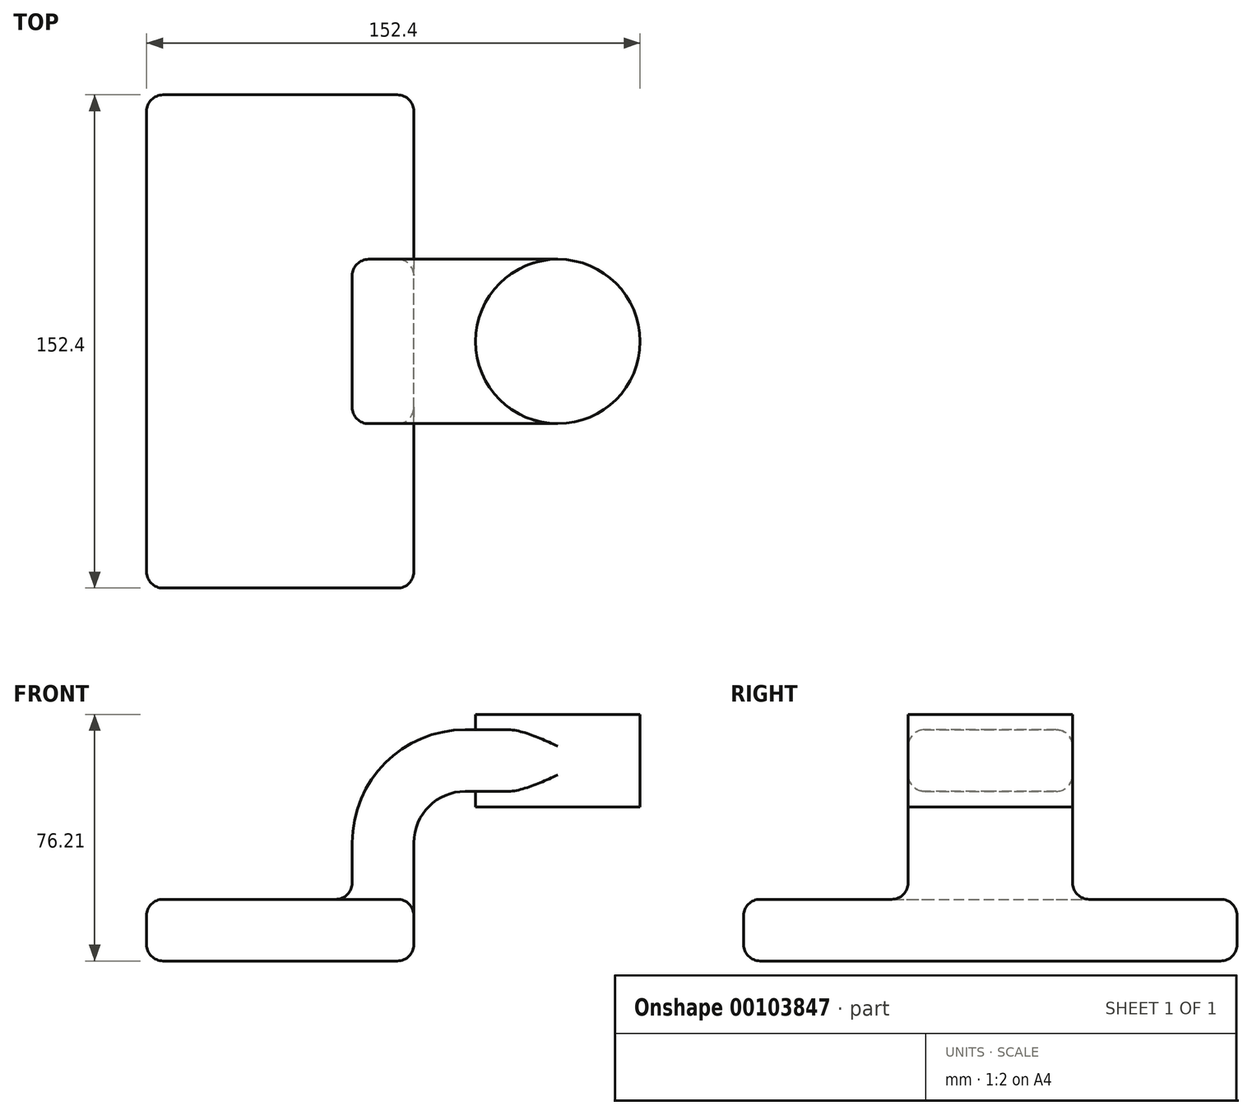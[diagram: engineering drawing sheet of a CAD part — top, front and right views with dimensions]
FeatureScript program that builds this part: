
annotation { "Feature Type Name" : "Feature", "Feature Type Description" : "" }
export const myFeature = defineFeature(function(context is Context, id is Id, definition is map)
    precondition{}
    {
        {
            var Q0;
            Q0=qCreatedBy(makeId("Front.planeOp"),FACE);
            var sketch = newSketch(context, id + "F0", { "sketchPlane" : qUnion([Q0])});
            skLineSegment(sketch, "E0.bottom", {"start": v(41.28, -9.52) * mm, "end": v(-41.27, -9.52) * mm});
            skLineSegment(sketch, "E0.top", {"start": v(41.27, 9.53) * mm, "end": v(-41.28, 9.53) * mm});
            skLineSegment(sketch, "E0.left", {"start": v(41.28, -9.52) * mm, "end": v(41.28, 9.53) * mm});
            skLineSegment(sketch, "E0.right", {"start": v(-41.27, -9.52) * mm, "end": v(-41.28, 9.53) * mm});
            skPoint(sketch, "E0.middle", {"position": v(0, 0) * mm});
            skLineSegment(sketch, "E1.bottom", {"start": v(111.13, 38.1) * mm, "end": v(60.33, 38.1) * mm});
            skLineSegment(sketch, "E1.top", {"start": v(111.12, 66.68) * mm, "end": v(60.33, 66.68) * mm});
            skLineSegment(sketch, "E1.left", {"start": v(111.13, 38.1) * mm, "end": v(111.13, 66.68) * mm});
            skLineSegment(sketch, "E1.right", {"start": v(60.33, 38.1) * mm, "end": v(60.33, 66.68) * mm});
            skPoint(sketch, "E1.middle", {"position": v(85.73, 52.39) * mm});
            skLineSegment(sketch, "E2", {"start": v(41.27, 9.53) * mm, "end": v(41.27, 27) * mm});
            skArc(sketch, "E3", {"start": v(41.27, 27) * mm, "mid": v(45.92, 38.23) * mm, "end": v(57.15, 42.88) * mm});
            skLineSegment(sketch, "E4", {"start": v(57.15, 42.88) * mm, "end": v(85.73, 42.88) * mm});
            skLineSegment(sketch, "E5.0", {"start": v(57.15, 61.93) * mm, "end": v(85.73, 61.93) * mm});
            skArc(sketch, "E5.1", {"start": v(22.22, 27) * mm, "mid": v(32.45, 51.7) * mm, "end": v(57.15, 61.93) * mm});
            skLineSegment(sketch, "E5.2", {"start": v(22.23, 9.53) * mm, "end": v(22.23, 27) * mm});
            skLineSegment(sketch, "E6", {"start": v(85.73, 38.1) * mm, "end": v(85.73, 66.68) * mm});
            skSolve(sketch);
        }
        {
            var Q0;
            Q0=makeQuery(id+"F0.imprint","IMPRINT",FACE,{"disambiguationData":[TD([[makeQuery(id+"F0.imprint","IMPRINT",EDGE,{"derivedFrom":sQuery(id+"F0.wireOp",EDGE,"E0.bottom")}),-1.0]])]});
            extrude(context, id + "F1", {"entities" : qUnion([Q0]), "endBound" : BoundingType.SYMMETRIC, "depth" : 152.4 * mm});
        }
        {
            var Q0;
            {var subQ1=sQuery(id+"F0.wireOp",EDGE,"E2");Q0=makeQuery(id+"F0.imprint","IMPRINT",FACE,{"disambiguationData":[TD([[makeQuery(id+"F0.imprint","IMPRINT",EDGE,{"derivedFrom":subQ1}),1.0]])]});}
            var Q1;
            {var subQ0=sQuery(id+"F0.wireOp",EDGE,"E4");var subQ1=sQuery(id+"F0.wireOp",EDGE,"E1.right");var subQ2=makeQuery(id+"F0.imprint","INTERSECT",VERTEX,{"derivedFrom":[subQ1,subQ0]});Q1=makeQuery(id+"F0.imprint","IMPRINT",FACE,{"disambiguationData":[TD([[makeQuery(id+"F0.imprint","IMPRINT",EDGE,{"disambiguationData":[TD([[subQ2,-1.0]])],"derivedFrom":subQ1}),-1.0]])]});}
            extrude(context, id + "F2", {"entities" : qUnion([Q0, Q1]), "operationType" : NewBodyOperationType.ADD, "endBound" : BoundingType.SYMMETRIC, "depth" : 50.8 * mm});
        }
        {
            var Q0;
            {var subQ0=sQuery(id+"F0.wireOp",EDGE,"E1.left");Q0=makeQuery(id+"F0.imprint","IMPRINT",FACE,{"disambiguationData":[TD([[makeQuery(id+"F0.imprint","IMPRINT",EDGE,{"derivedFrom":subQ0}),1.0]])]});}
            var Q1;
            Q1=sQuery(id+"F0.wireOp",EDGE,"E6");
            revolve(context, id + "F3", {"operationType" : NewBodyOperationType.ADD, "entities" : qUnion([Q0]), "axis" : qUnion([Q1]), "revolveType" : RevolveType.FULL});
        }
        {
            var Q0;
            Q0=makeQuery(id+"F1.opExtrude","SWEPT_FACE",FACE,{"disambiguationData":[OSD([sQuery(id+"F0.wireOp",EDGE,"E0.top")])]});
            var Q1;
            Q1=makeQuery(id+"F2.opExtrude","CAP_FACE",FACE,{"disambiguationData":[OSD([sQuery(id+"F0.wireOp",EDGE,"E0.top"),sQuery(id+"F0.wireOp",EDGE,"E2"),sQuery(id+"F0.wireOp",EDGE,"E3"),sQuery(id+"F0.wireOp",EDGE,"E4"),sQuery(id+"F0.wireOp",EDGE,"E5.0"),sQuery(id+"F0.wireOp",EDGE,"E5.1"),sQuery(id+"F0.wireOp",EDGE,"E5.2"),sQuery(id+"F0.wireOp",EDGE,"E6")])],"isStart":false});
            var Q2;
            Q2=makeQuery(id+"F2.opExtrude","CAP_FACE",FACE,{"disambiguationData":[OSD([sQuery(id+"F0.wireOp",EDGE,"E0.top"),sQuery(id+"F0.wireOp",EDGE,"E2"),sQuery(id+"F0.wireOp",EDGE,"E3"),sQuery(id+"F0.wireOp",EDGE,"E4"),sQuery(id+"F0.wireOp",EDGE,"E5.0"),sQuery(id+"F0.wireOp",EDGE,"E5.1"),sQuery(id+"F0.wireOp",EDGE,"E5.2"),sQuery(id+"F0.wireOp",EDGE,"E6")])],"isStart":true});
            var Q3;
            Q3=makeQuery(id+"F1.opExtrude","CAP_FACE",FACE,{"disambiguationData":[OSD([sQuery(id+"F0.wireOp",EDGE,"E0.bottom"),sQuery(id+"F0.wireOp",EDGE,"E0.top"),sQuery(id+"F0.wireOp",EDGE,"E0.left"),sQuery(id+"F0.wireOp",EDGE,"E0.right")])],"isStart":true});
            var Q4;
            Q4=makeQuery(id+"F1.opExtrude","SWEPT_FACE",FACE,{"disambiguationData":[OSD([sQuery(id+"F0.wireOp",EDGE,"E0.right")])]});
            var Q5;
            Q5=makeQuery(id+"F1.opExtrude","CAP_EDGE",EDGE,{"disambiguationData":[OSD([sQuery(id+"F0.wireOp",EDGE,"E0.bottom")])],"isStart":false});
            var Q6;
            Q6=makeQuery(id+"F2.boolean.opBoolean","MERGE",FACE,{"derivedFrom":[makeQuery(id+"F1.opExtrude","SWEPT_FACE",FACE,{"disambiguationData":[OSD([sQuery(id+"F0.wireOp",EDGE,"E0.left")])]}),makeQuery(id+"F2.opExtrude","SWEPT_FACE",FACE,{"disambiguationData":[OSD([sQuery(id+"F0.wireOp",EDGE,"E2")])]})]});
            fillet(context, id + "F4", {"entities" : qUnion([Q0, Q1, Q2, Q3, Q4, Q5, Q6]), "radius" : 5.08 * mm, "tangentPropagation" : true, "allowEdgeOverflow" : false});
        }
    });
